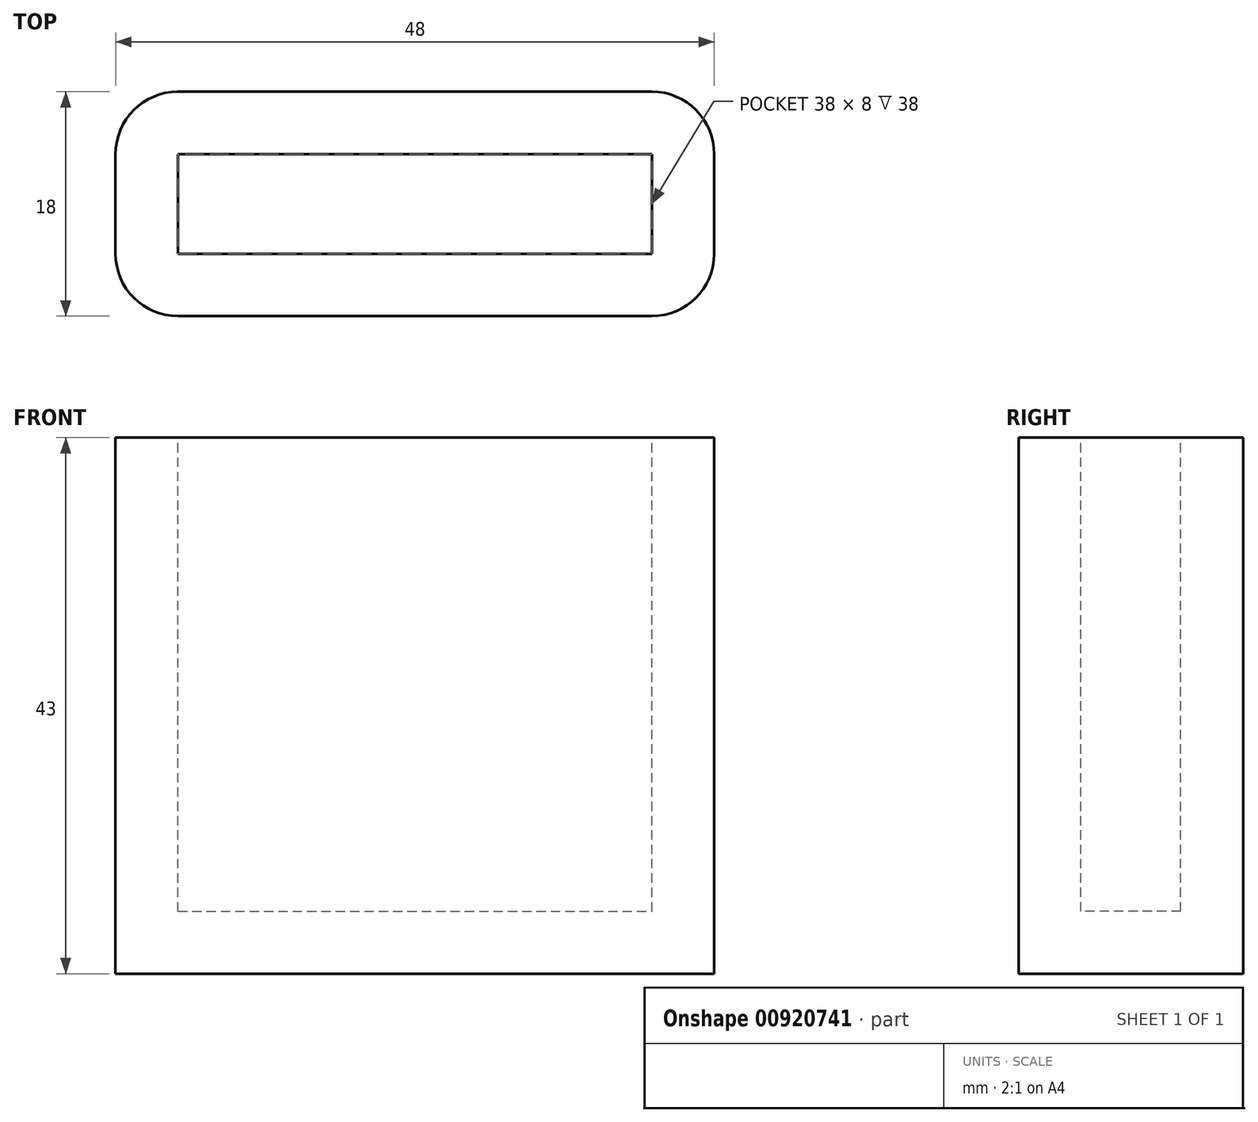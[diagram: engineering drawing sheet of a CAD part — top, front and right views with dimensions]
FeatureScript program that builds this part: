
annotation { "Feature Type Name" : "Feature", "Feature Type Description" : "" }
export const myFeature = defineFeature(function(context is Context, id is Id, definition is map)
    precondition{}
    {
        {
            var Q0;
            Q0=qCreatedBy(makeId("Top.planeOp"),FACE);
            var sketch = newSketch(context, id + "F0", { "sketchPlane" : qUnion([Q0])});
            skLineSegment(sketch, "E0.bottom", {"start": v(-26.46, 8.59) * mm, "end": v(21.54, 8.59) * mm});
            skLineSegment(sketch, "E0.top", {"start": v(-26.46, -9.41) * mm, "end": v(21.54, -9.41) * mm});
            skLineSegment(sketch, "E0.left", {"start": v(-26.46, 8.59) * mm, "end": v(-26.46, -9.41) * mm});
            skLineSegment(sketch, "E0.right", {"start": v(21.54, 8.59) * mm, "end": v(21.54, -9.41) * mm});
            skSolve(sketch);
        }
        {
            var Q0;
            Q0=makeQuery(id+"F0.imprint","IMPRINT",FACE,{"disambiguationData":[TD([[makeQuery(id+"F0.imprint","IMPRINT",EDGE,{"derivedFrom":sQuery(id+"F0.wireOp",EDGE,"E0.bottom")}),-1.0]])]});
            extrude(context, id + "F1", {"entities" : qUnion([Q0]), "depth" : 43 * mm, "offsetDistance" : 25 * mm});
        }
        {
            var Q0;
            Q0=makeQuery(id+"F1.opExtrude","CAP_FACE",FACE,{"disambiguationData":[OSD([sQuery(id+"F0.wireOp",EDGE,"E0.bottom"),sQuery(id+"F0.wireOp",EDGE,"E0.top"),sQuery(id+"F0.wireOp",EDGE,"E0.left"),sQuery(id+"F0.wireOp",EDGE,"E0.right")])],"isStart":false});
            var sketch = newSketch(context, id + "F2", { "sketchPlane" : qUnion([Q0])});
            skLineSegment(sketch, "E1.bottom", {"start": v(-21.46, 3.59) * mm, "end": v(16.54, 3.59) * mm});
            skLineSegment(sketch, "E1.top", {"start": v(-21.46, -4.41) * mm, "end": v(16.54, -4.41) * mm});
            skLineSegment(sketch, "E1.left", {"start": v(-21.46, 3.59) * mm, "end": v(-21.46, -4.41) * mm});
            skLineSegment(sketch, "E1.right", {"start": v(16.54, 3.59) * mm, "end": v(16.54, -4.41) * mm});
            skSolve(sketch);
        }
        {
            var Q0;
            Q0=makeQuery(id+"F2.imprint","IMPRINT",FACE,{"disambiguationData":[TD([[makeQuery(id+"F2.imprint","IMPRINT",EDGE,{"derivedFrom":sQuery(id+"F2.wireOp",EDGE,"E1.bottom")}),-1.0]])]});
            extrude(context, id + "F3", {"entities" : qUnion([Q0]), "operationType" : NewBodyOperationType.REMOVE, "oppositeDirection" : true, "depth" : 38 * mm, "offsetDistance" : 25 * mm});
        }
        {
            var Q0;
            Q0=makeQuery(id+"F1.opExtrude","SWEPT_EDGE",EDGE,{"disambiguationData":[OSD([sQuery(id+"F0.wireOp",EDGE,"E0.top"),sQuery(id+"F0.wireOp",EDGE,"E0.left")])]});
            var Q1;
            Q1=makeQuery(id+"F1.opExtrude","SWEPT_EDGE",EDGE,{"disambiguationData":[OSD([sQuery(id+"F0.wireOp",EDGE,"E0.top"),sQuery(id+"F0.wireOp",EDGE,"E0.right")])]});
            var Q2;
            Q2=makeQuery(id+"F1.opExtrude","SWEPT_EDGE",EDGE,{"disambiguationData":[OSD([sQuery(id+"F0.wireOp",EDGE,"E0.bottom"),sQuery(id+"F0.wireOp",EDGE,"E0.right")])]});
            var Q3;
            Q3=makeQuery(id+"F1.opExtrude","SWEPT_EDGE",EDGE,{"disambiguationData":[OSD([sQuery(id+"F0.wireOp",EDGE,"E0.bottom"),sQuery(id+"F0.wireOp",EDGE,"E0.left")])]});
            fillet(context, id + "F4", {"entities" : qUnion([Q0, Q1, Q2, Q3]), "radius" : 5 * mm, "tangentPropagation" : true, "allowEdgeOverflow" : false});
        }
    });
